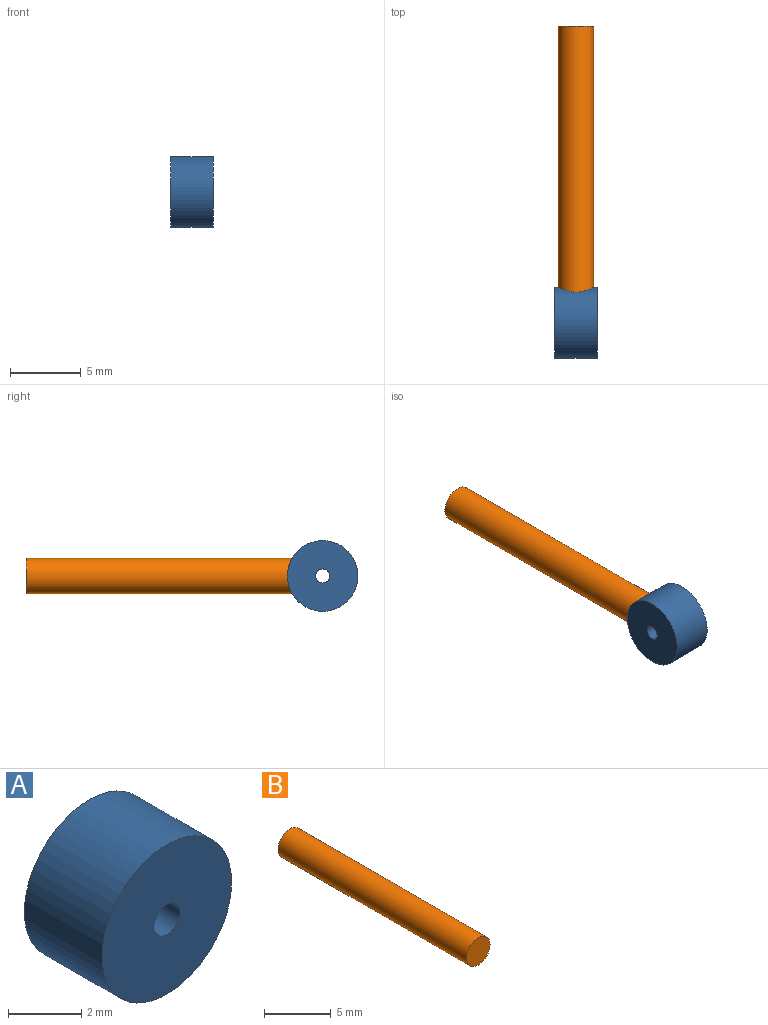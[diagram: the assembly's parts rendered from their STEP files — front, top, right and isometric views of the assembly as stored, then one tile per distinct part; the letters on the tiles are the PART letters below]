
ASSEMBLY  parts=2 mates=1
PART A: 6 faces, bbox 5x3x5 mm
  f0: cylinder r=0.5mm len=3mm, axis (0,1,0), area 9mm2, adj f2,f3,f5
  f1: cylinder r=2.5mm len=5mm, axis (0,1,0), area 42mm2, adj f2,f3,f4
  f2: plane 5x5mm, normal (0,-1,0), area 18.8mm2, adj f0,f1
  f3: plane 5x5mm, normal (0,1,0), area 18.8mm2, adj f0,f1
  f4: cylinder r=1.25mm len=2.5mm, axis (1,0,0), area 10.5mm2, adj f1,f5
  f5: cone r=0mm half-angle=59deg, axis (1,0,0), area 5.3mm2, adj f0,f4
PART B: 3 faces, bbox 2.5x20x2.5 mm
  f0: cylinder r=1.25mm len=20mm, axis (0,1,0), area 157.1mm2, adj f1,f2
  f1: plane 2.5x2.5mm, normal (0,-1,0), area 4.9mm2, adj f0
  f2: plane 2.5x2.5mm, normal (0,1,0), area 4.9mm2, adj f0
PLACE A rot(axis=(0,0,1),90deg) t=(-4.15,-20.79,0.36)mm
PLACE B t=(-2.65,0.21,0.36)mm
MATE fastened A.f4 <-> B.f0  axis (0,1,0) through (-2.65,-19.79,0.36)mm
